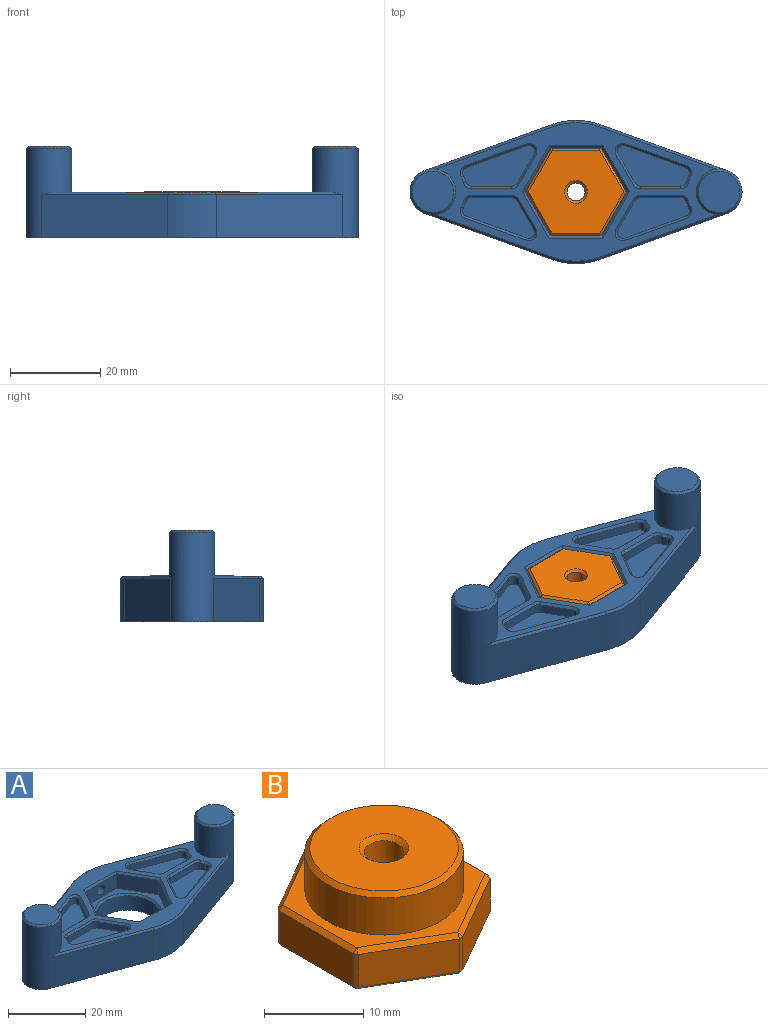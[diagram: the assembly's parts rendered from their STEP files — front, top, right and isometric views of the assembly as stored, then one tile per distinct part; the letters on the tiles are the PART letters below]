
ASSEMBLY  parts=2 mates=1
PART A: 104 faces, bbox 73.7x31.8x20.3 mm
  f0: cylinder r=5.08mm len=19.81mm, axis (0,0,-1), area 436mm2, adj f2,f5,f13,f14,f90,f93,f101
  f1: plane 9.14x9.14mm, normal (0,0,1), area 65.7mm2, adj f101
  f2: plane 73.66x31.75mm, normal (0,0,-1), area 1278.6mm2, adj f0,f3,f11,f12,f13,f14,f15,f16
  f3: cylinder r=5.08mm len=19.81mm, axis (0,0,-1), area 436mm2, adj f2,f5,f11,f16,f88,f91,f102
  f4: plane 9.14x9.14mm, normal (0,0,1), area 65.7mm2, adj f102
  f5: plane 62.44x30.73mm, normal (0,0,1), area 452.2mm2, adj f0,f3,f56,f57,f58,f59,f60,f61
  f6: plane 9.78x5.65mm, normal (-0.87,0.5,0), area 51.6mm2, adj f7,f17,f39,f98
  f7: plane 11.29x4.57mm, normal (0,1,0), area 51.6mm2, adj f6,f8,f39,f96
  f8: plane 9.78x5.65mm, normal (0.87,0.5,0), area 51.6mm2, adj f7,f9,f39,f95
  f9: plane 9.78x5.65mm, normal (0.87,-0.5,0), area 51.6mm2, adj f8,f10,f39,f97
  f10: plane 11.29x4.57mm, normal (0,-1,0), area 45.5mm2, adj f9,f17,f39,f99,f103
  f11: plane 28.08x10.15mm, normal (-0.34,-0.94,0), area 288.2mm2, adj f2,f3,f12,f91
  f12: cylinder r=15.88mm len=10.8mm, axis (0,0,-1), area 106.3mm2, adj f2,f11,f13,f92
  f13: plane 28.08x10.15mm, normal (0.34,-0.94,0), area 288.2mm2, adj f0,f2,f12,f93
  f14: plane 28.08x10.15mm, normal (0.34,0.94,0), area 288.2mm2, adj f0,f2,f15,f90
  f15: cylinder r=15.88mm len=10.8mm, axis (0,0,-1), area 100.2mm2, adj f2,f14,f16,f89,f103
  f16: plane 28.08x10.15mm, normal (-0.34,0.94,0), area 288.2mm2, adj f2,f3,f15,f88
  f17: plane 9.78x5.65mm, normal (-0.87,-0.5,0), area 51.6mm2, adj f6,f10,f39,f100
  f18: cylinder r=7.62mm len=2.03mm, axis (0,0,1), area 3.1mm2, adj f22,f52,f55,f75
  f19: plane 9x2.03mm, normal (0,1,0), area 18.3mm2, adj f22,f54,f55,f79
  f20: plane 6.51x3.76mm, normal (-0.87,0.5,0), area 15.3mm2, adj f22,f53,f54,f76
  f21: plane 13.44x4.86mm, normal (0.34,-0.94,0), area 29mm2, adj f22,f52,f53,f72
  f22: plane 15.98x9.06mm, normal (0,0,1), area 88.5mm2, adj f18,f19,f20,f21,f52,f53,f54,f55
  f23: plane 9x2.03mm, normal (0,-1,0), area 18.3mm2, adj f27,f40,f43,f56
  f24: plane 6.51x3.76mm, normal (0.87,-0.5,0), area 15.3mm2, adj f27,f42,f43,f60
  f25: plane 13.44x4.86mm, normal (-0.34,0.94,0), area 29mm2, adj f27,f41,f42,f63
  f26: cylinder r=7.62mm len=2.03mm, axis (0,0,1), area 3.2mm2, adj f27,f40,f41,f59
  f27: plane 15.98x9.07mm, normal (0,0,1), area 88.6mm2, adj f23,f24,f25,f26,f40,f41,f42,f43
  f28: cylinder r=7.62mm len=2.03mm, axis (0,0,1), area 3.1mm2, adj f32,f44,f47,f83
  f29: plane 13.44x4.86mm, normal (0.34,0.94,0), area 29mm2, adj f32,f46,f47,f87
  f30: plane 6.51x3.76mm, normal (-0.87,-0.5,0), area 15.3mm2, adj f32,f45,f46,f84
  f31: plane 9x2.03mm, normal (0,-1,0), area 18.3mm2, adj f32,f44,f45,f80
  f32: plane 15.98x9.06mm, normal (0,0,1), area 88.5mm2, adj f28,f29,f30,f31,f44,f45,f46,f47
  f33: plane 13.44x4.86mm, normal (-0.34,-0.94,0), area 29mm2, adj f37,f48,f51,f64
  f34: plane 6.51x3.76mm, normal (0.87,0.5,0), area 15.3mm2, adj f37,f48,f49,f67
  f35: plane 9x2.03mm, normal (0,1,0), area 18.3mm2, adj f37,f49,f50,f71
  f36: cylinder r=7.62mm len=2.03mm, axis (0,0,1), area 3.2mm2, adj f37,f50,f51,f68
  f37: plane 15.98x9.07mm, normal (0,0,1), area 88.6mm2, adj f33,f34,f35,f36,f48,f49,f50,f51
  f38: cylinder r=8.19mm len=16.38mm, axis (0,0,-1), area 235.3mm2, adj f2,f94
  f39: plane 22.58x19.56mm, normal (0,0,1), area 93.5mm2, adj f6,f7,f8,f9,f10,f17,f94
  f40: cylinder r=1.27mm len=2.03mm, axis (0,0,1), area 3.3mm2, adj f23,f26,f27,f57
  f41: cylinder r=1.27mm len=2.03mm, axis (0,0,1), area 4.4mm2, adj f25,f26,f27,f61
  f42: cylinder r=1.27mm len=2.03mm, axis (0,0,-1), area 6.3mm2, adj f24,f25,f27,f62
  f43: cylinder r=1.27mm len=2.03mm, axis (0,0,-1), area 2.7mm2, adj f23,f24,f27,f58
  f44: cylinder r=1.27mm len=2.03mm, axis (0,0,1), area 3.3mm2, adj f28,f31,f32,f81
  f45: cylinder r=1.27mm len=2.03mm, axis (0,0,-1), area 2.7mm2, adj f30,f31,f32,f82
  f46: cylinder r=1.27mm len=2.03mm, axis (0,0,1), area 6.3mm2, adj f29,f30,f32,f86
  f47: cylinder r=1.27mm len=2.03mm, axis (0,0,1), area 4.4mm2, adj f28,f29,f32,f85
  f48: cylinder r=1.27mm len=2.03mm, axis (0,0,-1), area 6.3mm2, adj f33,f34,f37,f65
  f49: cylinder r=1.27mm len=2.03mm, axis (0,0,1), area 2.7mm2, adj f34,f35,f37,f69
  f50: cylinder r=1.27mm len=2.03mm, axis (0,0,1), area 3.3mm2, adj f35,f36,f37,f70
  f51: cylinder r=1.27mm len=2.03mm, axis (0,0,1), area 4.4mm2, adj f33,f36,f37,f66
  f52: cylinder r=1.27mm len=2.03mm, axis (0,0,1), area 4.4mm2, adj f18,f21,f22,f73
  f53: cylinder r=1.27mm len=2.03mm, axis (0,0,-1), area 6.3mm2, adj f20,f21,f22,f74
  f54: cylinder r=1.27mm len=2.03mm, axis (0,0,1), area 2.7mm2, adj f19,f20,f22,f78
  f55: cylinder r=1.27mm len=2.03mm, axis (0,0,1), area 3.3mm2, adj f18,f19,f22,f77
  f56: plane 9x0.54mm, normal (0,-0.71,0.71), area 6.5mm2, adj f5,f23,f57,f58
  f57: cone r=1.78mm half-angle=45deg, axis (0,0,1), area 1.4mm2, adj f5,f40,f56,f59
  f58: cone r=1.78mm half-angle=45deg, axis (0,0,1), area 1.1mm2, adj f5,f43,f56,f60
  f59: cone r=7.11mm half-angle=45deg, axis (0,0,-1), area 1.1mm2, adj f5,f26,f57,f61
  f60: plane 6.76x4.2mm, normal (0.61,-0.35,0.71), area 5.4mm2, adj f5,f24,f58,f62
  f61: cone r=1.78mm half-angle=45deg, axis (0,0,1), area 1.9mm2, adj f5,f41,f59,f63
  f62: cone r=1.78mm half-angle=45deg, axis (0,0,1), area 2.7mm2, adj f5,f42,f60,f63
  f63: plane 13.61x5.34mm, normal (-0.24,0.66,0.71), area 10.3mm2, adj f5,f25,f61,f62
  f64: plane 13.61x5.34mm, normal (-0.24,-0.66,0.71), area 10.3mm2, adj f5,f33,f65,f66
  f65: cone r=1.78mm half-angle=45deg, axis (0,0,1), area 2.7mm2, adj f5,f48,f64,f67
  f66: cone r=1.78mm half-angle=45deg, axis (0,0,1), area 1.9mm2, adj f5,f51,f64,f68
  f67: plane 6.76x4.2mm, normal (0.61,0.35,0.71), area 5.4mm2, adj f5,f34,f65,f69
  f68: cone r=7.11mm half-angle=45deg, axis (0,0,-1), area 1.1mm2, adj f5,f36,f66,f70
  f69: cone r=1.78mm half-angle=45deg, axis (0,0,1), area 1.1mm2, adj f5,f49,f67,f71
  f70: cone r=1.78mm half-angle=45deg, axis (0,0,1), area 1.4mm2, adj f5,f50,f68,f71
  f71: plane 9x0.54mm, normal (0,0.71,0.71), area 6.5mm2, adj f5,f35,f69,f70
  f72: plane 13.61x5.34mm, normal (0.24,-0.66,0.71), area 10.3mm2, adj f5,f21,f73,f74
  f73: cone r=1.78mm half-angle=45deg, axis (0,0,1), area 1.9mm2, adj f5,f52,f72,f75
  f74: cone r=1.78mm half-angle=45deg, axis (0,0,1), area 2.7mm2, adj f5,f53,f72,f76
  f75: cone r=7.11mm half-angle=45deg, axis (0,0,-1), area 1.1mm2, adj f5,f18,f73,f77
  f76: plane 6.76x4.2mm, normal (-0.61,0.35,0.71), area 5.4mm2, adj f5,f20,f74,f78
  f77: cone r=1.78mm half-angle=45deg, axis (0,0,1), area 1.4mm2, adj f5,f55,f75,f79
  f78: cone r=1.78mm half-angle=45deg, axis (0,0,1), area 1.1mm2, adj f5,f54,f76,f79
  f79: plane 9x0.52mm, normal (0,0.71,0.71), area 6.5mm2, adj f5,f19,f77,f78
  f80: plane 9x0.52mm, normal (0,-0.71,0.71), area 6.5mm2, adj f5,f31,f81,f82
  f81: cone r=1.78mm half-angle=45deg, axis (0,0,1), area 1.4mm2, adj f5,f44,f80,f83
  f82: cone r=1.78mm half-angle=45deg, axis (0,0,1), area 1.1mm2, adj f5,f45,f80,f84
  f83: cone r=7.11mm half-angle=45deg, axis (0,0,-1), area 1.1mm2, adj f5,f28,f81,f85
  f84: plane 6.76x4.2mm, normal (-0.61,-0.35,0.71), area 5.4mm2, adj f5,f30,f82,f86
  f85: cone r=1.78mm half-angle=45deg, axis (0,0,1), area 1.9mm2, adj f5,f47,f83,f87
  f86: cone r=1.78mm half-angle=45deg, axis (0,0,1), area 2.7mm2, adj f5,f46,f84,f87
  f87: plane 13.61x5.34mm, normal (0.24,0.66,0.71), area 10.3mm2, adj f5,f29,f85,f86
  f88: plane 28.25x10.15mm, normal (-0.24,0.66,0.71), area 20.4mm2, adj f3,f5,f16,f89
  f89: cone r=15.37mm half-angle=45deg, axis (0,0,-1), area 7.8mm2, adj f5,f15,f88,f90
  f90: plane 28.25x10.15mm, normal (0.24,0.66,0.71), area 20.4mm2, adj f0,f5,f14,f89
  f91: plane 28.25x10.15mm, normal (-0.24,-0.66,0.71), area 20.4mm2, adj f3,f5,f11,f92
  f92: cone r=15.37mm half-angle=45deg, axis (0,0,-1), area 7.8mm2, adj f5,f12,f91,f93
  f93: plane 28.25x10.15mm, normal (0.24,-0.66,0.71), area 20.4mm2, adj f0,f5,f13,f92
  f94: cone r=8.19mm half-angle=45deg, axis (0,0,1), area 38.1mm2, adj f38,f39
  f95: plane 10.29x6.23mm, normal (0.61,0.35,0.71), area 8.3mm2, adj f5,f8,f96,f97
  f96: plane 11.88x0.51mm, normal (0,0.71,0.71), area 8.3mm2, adj f5,f7,f95,f98
  f97: plane 10.29x6.23mm, normal (0.61,-0.35,0.71), area 8.3mm2, adj f5,f9,f95,f99
  f98: plane 10.29x6.23mm, normal (-0.61,0.35,0.71), area 8.3mm2, adj f5,f6,f96,f100
  f99: plane 11.88x0.51mm, normal (0,-0.71,0.71), area 8.3mm2, adj f5,f10,f97,f100
  f100: plane 10.29x6.23mm, normal (-0.61,-0.35,0.71), area 8.3mm2, adj f5,f17,f98,f99
  f101: cone r=4.57mm half-angle=45deg, axis (0,0,-1), area 21.8mm2, adj f0,f1
  f102: cone r=4.57mm half-angle=45deg, axis (0,0,-1), area 21.8mm2, adj f3,f4
  f103: cylinder r=1.4mm len=6.1mm, axis (0,-1,0), area 53.2mm2, adj f10,f15
PART B: 44 faces, bbox 19.3x22x10.2 mm
  f0: cylinder r=8mm len=16mm, axis (0,0,-1), area 229.8mm2, adj f8,f40
  f1: plane 14.99x14.99mm, normal (0,0,1), area 156.6mm2, adj f40,f43
  f2: plane 9.14x5.28mm, normal (0.5,-0.87,0), area 42.9mm2, adj f10,f13,f17,f18
  f3: plane 10.56x4.06mm, normal (1,0,0), area 42.9mm2, adj f18,f23,f27,f28
  f4: plane 9.14x5.28mm, normal (0.5,0.87,0), area 42.9mm2, adj f28,f33,f36,f39
  f5: plane 9.14x5.28mm, normal (-0.5,0.87,0), area 42.9mm2, adj f25,f34,f35,f39
  f6: plane 10.56x4.06mm, normal (-1,0,0), area 42.9mm2, adj f15,f24,f25,f26
  f7: plane 9.14x5.28mm, normal (-0.5,-0.87,0), area 42.9mm2, adj f10,f14,f15,f16
  f8: plane 21.12x18.29mm, normal (0,0,1), area 88.5mm2, adj f0,f13,f14,f23,f24,f33,f34
  f9: plane 21.12x18.29mm, normal (0,0,-1), area 269.9mm2, adj f16,f17,f26,f27,f35,f36,f42
  f10: plane 4.06x0.51mm, normal (0,-1,0), area 2.1mm2, adj f2,f7,f11,f12
  f11: plane 0.51x0.51mm, normal (0,-0.76,0.65), area 0.2mm2, adj f10,f13,f14
  f12: plane 0.51x0.51mm, normal (0,-0.76,-0.65), area 0.2mm2, adj f10,f16,f17
  f13: plane 9.4x5.72mm, normal (0.35,-0.61,0.71), area 7.6mm2, adj f2,f8,f11,f19
  f14: plane 9.4x5.72mm, normal (-0.35,-0.61,0.71), area 7.6mm2, adj f7,f8,f11,f20
  f15: plane 4.06x0.44mm, normal (-0.87,-0.5,0), area 2.1mm2, adj f6,f7,f20,f21
  f16: plane 9.4x5.72mm, normal (-0.35,-0.61,-0.71), area 7.6mm2, adj f7,f9,f12,f21
  f17: plane 9.4x5.72mm, normal (0.35,-0.61,-0.71), area 7.6mm2, adj f2,f9,f12,f22
  f18: plane 4.06x0.44mm, normal (0.87,-0.5,0), area 2.1mm2, adj f2,f3,f19,f22
  f19: plane 0.51x0.51mm, normal (0.65,-0.38,0.65), area 0.2mm2, adj f13,f18,f23
  f20: plane 0.51x0.51mm, normal (-0.65,-0.38,0.65), area 0.2mm2, adj f14,f15,f24
  f21: plane 0.51x0.51mm, normal (-0.65,-0.38,-0.65), area 0.2mm2, adj f15,f16,f26
  f22: plane 0.51x0.51mm, normal (0.65,-0.38,-0.65), area 0.2mm2, adj f17,f18,f27
  f23: plane 10.56x0.51mm, normal (0.71,0,0.71), area 7.6mm2, adj f3,f8,f19,f29
  f24: plane 10.56x0.51mm, normal (-0.71,0,0.71), area 7.6mm2, adj f6,f8,f20,f30
  f25: plane 4.06x0.44mm, normal (-0.87,0.5,0), area 2.1mm2, adj f5,f6,f30,f31
  f26: plane 10.56x0.51mm, normal (-0.71,0,-0.71), area 7.6mm2, adj f6,f9,f21,f31
  f27: plane 10.56x0.51mm, normal (0.71,0,-0.71), area 7.6mm2, adj f3,f9,f22,f32
  f28: plane 4.06x0.44mm, normal (0.87,0.5,0), area 2.1mm2, adj f3,f4,f29,f32
  f29: plane 0.51x0.51mm, normal (0.65,0.38,0.65), area 0.2mm2, adj f23,f28,f33
  f30: plane 0.51x0.51mm, normal (-0.65,0.38,0.65), area 0.2mm2, adj f24,f25,f34
  f31: plane 0.51x0.51mm, normal (-0.65,0.38,-0.65), area 0.2mm2, adj f25,f26,f35
  f32: plane 0.51x0.51mm, normal (0.65,0.38,-0.65), area 0.2mm2, adj f27,f28,f36
  f33: plane 9.4x5.72mm, normal (0.35,0.61,0.71), area 7.6mm2, adj f4,f8,f29,f37
  f34: plane 9.4x5.72mm, normal (-0.35,0.61,0.71), area 7.6mm2, adj f5,f8,f30,f37
  f35: plane 9.4x5.72mm, normal (-0.35,0.61,-0.71), area 7.6mm2, adj f5,f9,f31,f38
  f36: plane 9.4x5.72mm, normal (0.35,0.61,-0.71), area 7.6mm2, adj f4,f9,f32,f38
  f37: plane 0.51x0.51mm, normal (0,0.76,0.65), area 0.2mm2, adj f33,f34,f39
  f38: plane 0.51x0.51mm, normal (0,0.76,-0.65), area 0.2mm2, adj f35,f36,f39
  f39: plane 4.06x0.51mm, normal (0,1,0), area 2.1mm2, adj f4,f5,f37,f38
  f40: cone r=7.49mm half-angle=45deg, axis (0,0,-1), area 35mm2, adj f0,f1
  f41: cylinder r=2mm len=9.14mm, axis (0,0,1), area 114.9mm2, adj f42,f43
  f42: cone r=2.51mm half-angle=45deg, axis (0,0,-1), area 10.2mm2, adj f9,f41
  f43: cone r=2mm half-angle=45deg, axis (0,0,1), area 10.2mm2, adj f1,f41
PLACE A t=(15.93,-3.08,-22.55)mm fixed
PLACE B rot(axis=(0.71,0.71,0),180deg) t=(47.69,46.05,-12.39)mm
MATE fastened B.f0 <-> A.f38  axis (0,0,-1) through (15.93,-3.08,-22.55)mm
